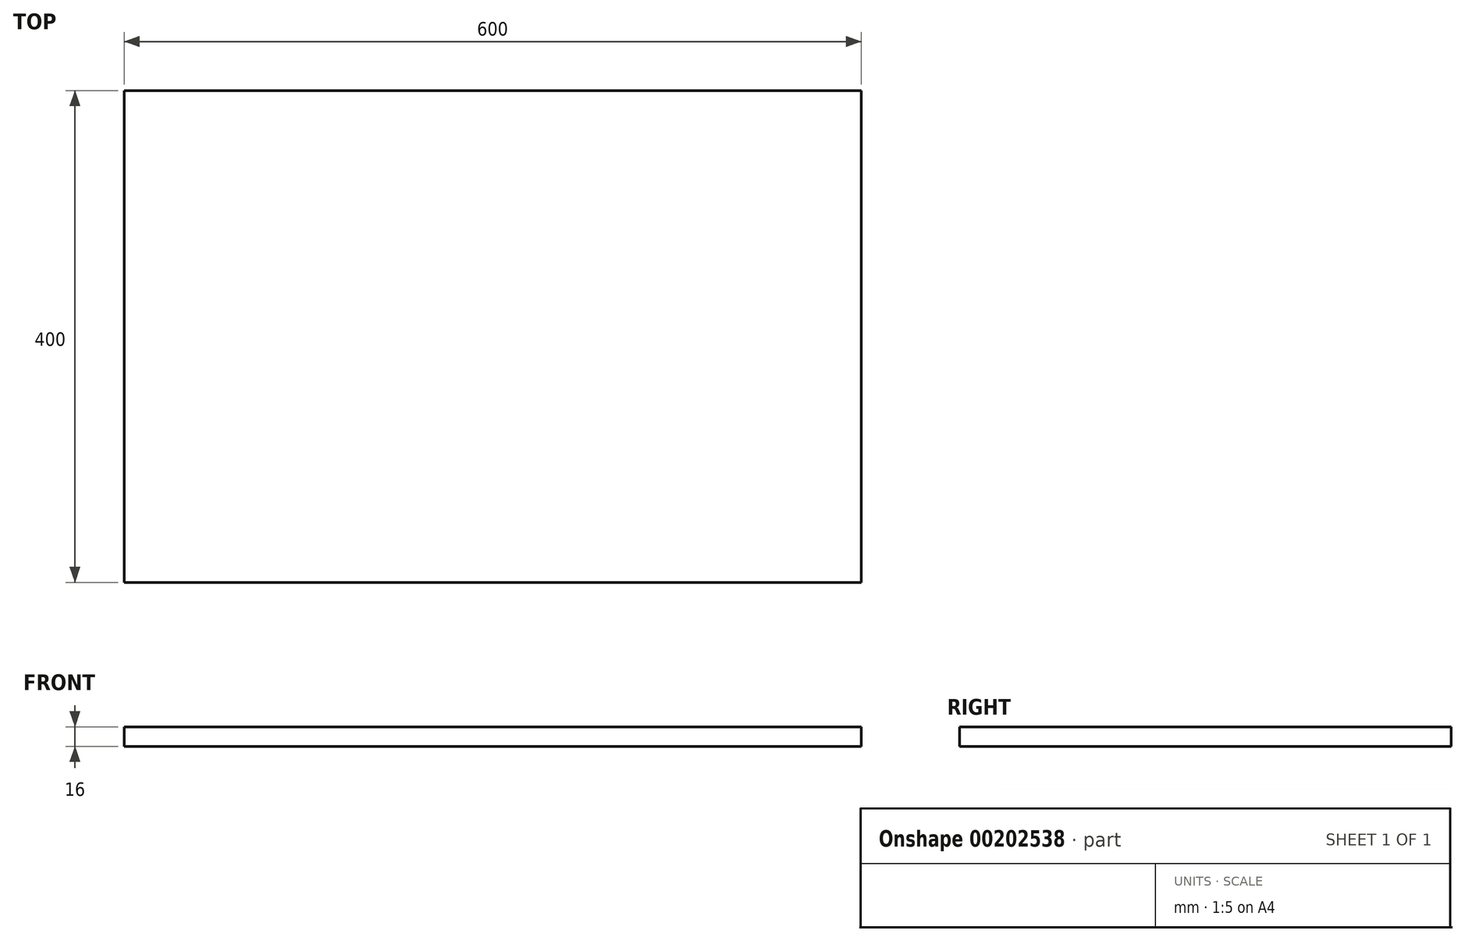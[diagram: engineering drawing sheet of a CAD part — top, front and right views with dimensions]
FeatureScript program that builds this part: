
annotation { "Feature Type Name" : "Feature", "Feature Type Description" : "" }
export const myFeature = defineFeature(function(context is Context, id is Id, definition is map)
    precondition{}
    {
        {
            var Q0;
            Q0=qCreatedBy(makeId("Top.planeOp"),FACE);
            var sketch = newSketch(context, id + "F0", { "sketchPlane" : qUnion([Q0])});
            skLineSegment(sketch, "E0.bottom", {"start": v(-276.3, -87.4) * mm, "end": v(323.7, -87.4) * mm});
            skLineSegment(sketch, "E0.top", {"start": v(-276.3, 312.6) * mm, "end": v(323.7, 312.6) * mm});
            skLineSegment(sketch, "E0.left", {"start": v(-276.3, -87.4) * mm, "end": v(-276.3, 312.6) * mm});
            skLineSegment(sketch, "E0.right", {"start": v(323.7, -87.4) * mm, "end": v(323.7, 312.6) * mm});
            skSolve(sketch);
        }
        {
            var Q0;
            Q0=makeQuery(id+"F0.imprint","IMPRINT",FACE,{"disambiguationData":[TD([[makeQuery(id+"F0.imprint","IMPRINT",EDGE,{"derivedFrom":sQuery(id+"F0.wireOp",EDGE,"E0.bottom")}),1.0]])]});
            extrude(context, id + "F1", {"entities" : qUnion([Q0]), "depth" : 16 * mm});
        }
    });
